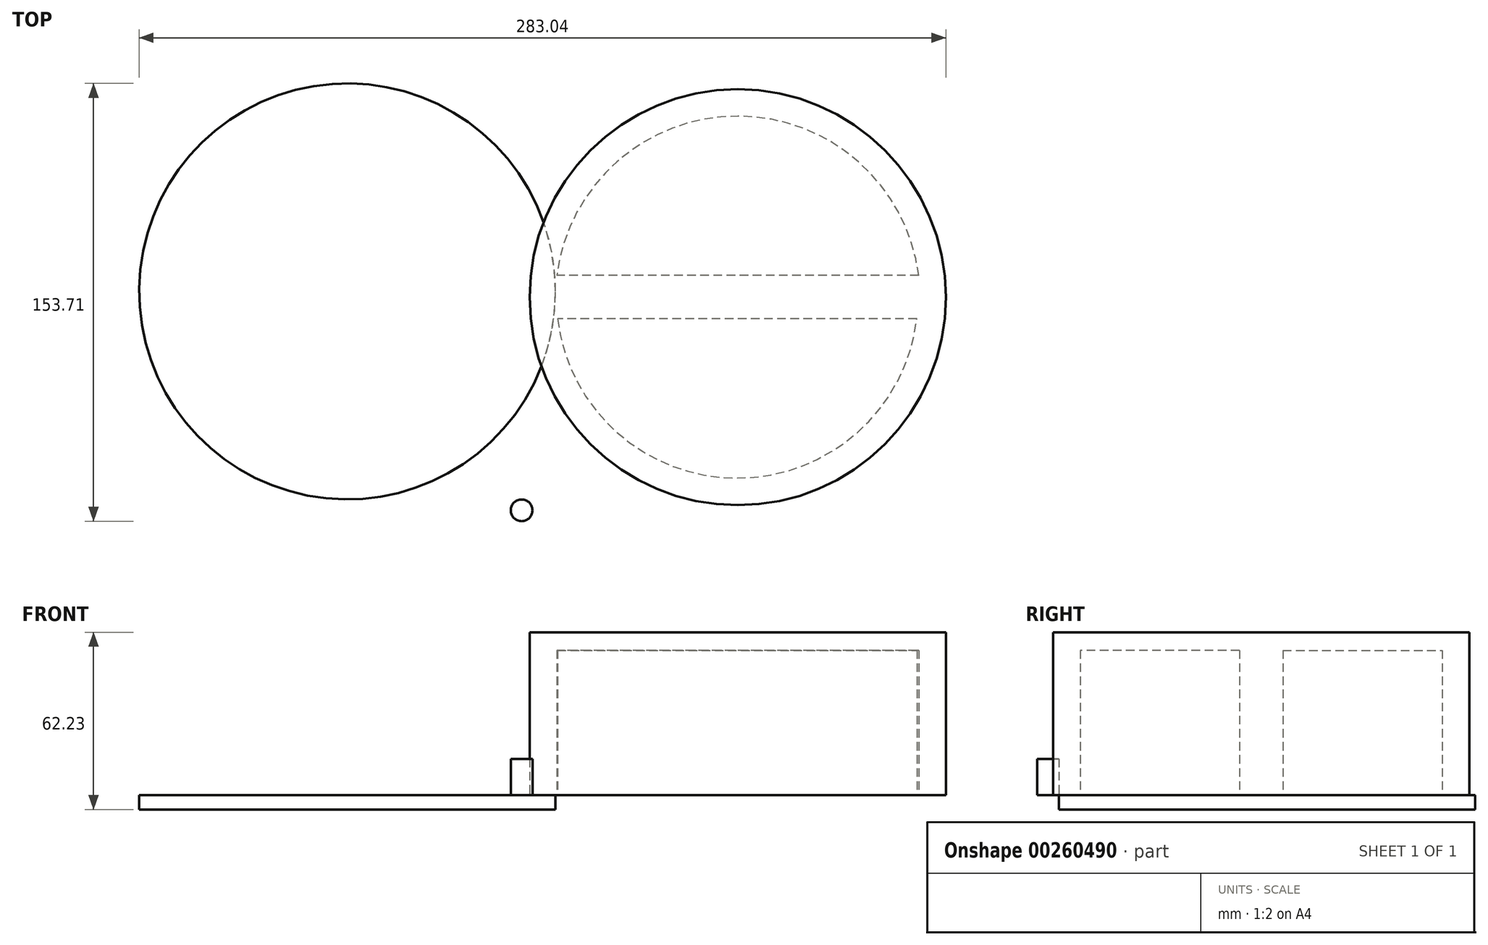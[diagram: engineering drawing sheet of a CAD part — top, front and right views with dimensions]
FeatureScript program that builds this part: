
annotation { "Feature Type Name" : "Feature", "Feature Type Description" : "" }
export const myFeature = defineFeature(function(context is Context, id is Id, definition is map)
    precondition{}
    {
        {
            var Q0;
            Q0=qCreatedBy(makeId("Top.planeOp"),FACE);
            var sketch = newSketch(context, id + "F0", { "sketchPlane" : qUnion([Q0])});
            skCircle(sketch, "E0", {"center": v(0, 0) * mm, "radius": 73.02 * mm});
            skPoint(sketch, "E1.first.point", {"position": v(73.02, 0) * mm});
            skPoint(sketch, "E1.second.point", {"position": v(159.06, -115.69) * mm});
            skPoint(sketch, "E1.third.point", {"position": v(169.77, -101.58) * mm});
            skSolve(sketch);
        }
        {
            var Q0;
            Q0 = qSketchRegion(id + "F0", true);
            extrude(context, id + "F1", {"entities" : qUnion([Q0]), "depth" : 57.15 * mm});
        }
        {
            var Q0;
            Q0=qCreatedBy(makeId("Top.planeOp"),FACE);
            var sketch = newSketch(context, id + "F2", { "sketchPlane" : qUnion([Q0])});
            skCircle(sketch, "E2", {"center": v(-136.98, 2.06) * mm, "radius": 73.03 * mm});
            skPoint(sketch, "E2.first.point", {"position": v(-63.98, 0) * mm});
            skPoint(sketch, "E2.second.point", {"position": v(-116.1, 72.04) * mm});
            skPoint(sketch, "E2.third.point", {"position": v(-128.99, -70.53) * mm});
            skSolve(sketch);
        }
        {
            var Q0;
            Q0=makeQuery(id+"F2.imprint","IMPRINT",FACE,{"disambiguationData":[TD([[makeQuery(id+"F2.imprint","IMPRINT",EDGE,{"derivedFrom":sQuery(id+"F2.wireOp",EDGE,"E2")}),1.0]])]});
            var Q1;
            Q1=sQuery(id+"F2.wireOp",EDGE,"E2");
            extrude(context, id + "F3", {"entities" : qUnion([Q0]), "surfaceEntities" : qUnion([Q1]), "oppositeDirection" : true, "depth" : 5.08 * mm});
        }
        {
            var Q0;
            Q0=qCreatedBy(makeId("Top.planeOp"),FACE);
            var sketch = newSketch(context, id + "F4", { "sketchPlane" : qUnion([Q0])});
            skArc(sketch, "E3", {"start": v(-63.67, 0) * mm, "mid": v(-0.17, -63.5) * mm, "end": v(63.33, 0) * mm});
            skLineSegment(sketch, "E4", {"start": v(-63.67, 0) * mm, "end": v(63.33, 0) * mm});
            skLineSegment(sketch, "E5", {"start": v(62.87, -7.62) * mm, "end": v(-63.21, -7.62) * mm});
            skLineSegment(sketch, "E6", {"start": v(0, 0) * mm, "end": v(0, -7.62) * mm});
            skArc(sketch, "E7", {"start": v(63.33, 0) * mm, "mid": v(-0.17, 63.5) * mm, "end": v(-63.67, 0) * mm});
            skSolve(sketch);
        }
        {
            var Q0;
            {var subQ0=sQuery(id+"F4.wireOp",EDGE,"E5");Q0=makeQuery(id+"F4.imprint","IMPRINT",FACE,{"disambiguationData":[TD([[makeQuery(id+"F4.imprint","IMPRINT",EDGE,{"derivedFrom":subQ0}),1.0]])]});}
            extrude(context, id + "F5", {"entities" : qUnion([Q0]), "operationType" : NewBodyOperationType.REMOVE, "depth" : 50.8 * mm});
        }
        {
            var Q0;
            Q0=qCreatedBy(makeId("Top.planeOp"),FACE);
            var sketch = newSketch(context, id + "F6", { "sketchPlane" : qUnion([Q0])});
            skLineSegment(sketch, "E8", {"start": v(0, 0) * mm, "end": v(0, 7.62) * mm});
            skLineSegment(sketch, "E9", {"start": v(0, 7.62) * mm, "end": v(63.5, 7.62) * mm});
            skLineSegment(sketch, "E10", {"start": v(0, 7.62) * mm, "end": v(-63.5, 7.62) * mm});
            skArc(sketch, "E11", {"start": v(63.5, 7.62) * mm, "mid": v(0, 63.58) * mm, "end": v(-63.5, 7.62) * mm});
            skSolve(sketch);
        }
        {
            var Q0;
            Q0 = qSketchRegion(id + "F6", true);
            extrude(context, id + "F7", {"entities" : qUnion([Q0]), "operationType" : NewBodyOperationType.REMOVE, "depth" : 50.8 * mm});
        }
        {
            var Q0;
            Q0=qCreatedBy(makeId("Top.planeOp"),FACE);
            var sketch = newSketch(context, id + "F8", { "sketchPlane" : qUnion([Q0])});
            skCircle(sketch, "E12", {"center": v(-75.82, -74.82) * mm, "radius": 3.81 * mm});
            skSolve(sketch);
        }
        {
            var Q0;
            Q0 = qSketchRegion(id + "F8", true);
            extrude(context, id + "F9", {"entities" : qUnion([Q0]), "depth" : 12.7 * mm});
        }
    });
